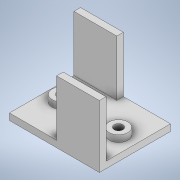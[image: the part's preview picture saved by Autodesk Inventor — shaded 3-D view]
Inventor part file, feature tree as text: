
AUTODESK INVENTOR PART (.ipt)
format: ipt  version: 2020 (Build 240168000, 168)  size: 171,520 bytes
history: native  units: in
note: dims shown in document units (in); Inventor stores cm internally (conversion verified against a paired STEP export)
features: extrude x7, sketch x7
ambient origin geometry x8: Origin, YZ Plane, XZ Plane, XY Plane, X Axis, Y Axis, Z Axis, Center Point
bodies: Solid1 (feature_tree)
feature tree (14):
  extrude  "Extrusion1"  Depth=1.2756in
  extrude  "Extrusion3"  Depth=0.1181in
  extrude  "Extrusion4"  Depth=1.0in TaperAngle=0.0deg
  extrude  "Extrusion5"  Depth=0.1181in TaperAngle=0.0deg
  extrude  "Extrusion6"  Depth=0.1181in TaperAngle=0.0deg
  extrude  "Extrusion7"  Depth=0.3346in
  extrude  "Extrusion8"  Depth=0.1181in
  sketch  "Sketch1"  dims[d0=1.6142in d1=1.2756in]
  sketch  "Sketch3"  dims[d2=0.1181in d3=0.0in d8=0.1181in]
  sketch  "Sketch4"  dims[d9=0.1181in d10=1.0in d11=0.0in]
  sketch  "Sketch5"  dims[d12=0.8465in d13=0.1181in d14=0.0in]
  sketch  "Sketch6"  dims[d15=0.8465in d16=0.1181in d17=0.0in]
  sketch  "Sketch7"  dims[d20=0.3346in d21=0.3346in]
  sketch  "Sketch8"  dims[d22=0.1181in d23=0.0in d24=0.1575in d25=0.1575in d26=0.2362in d27=0.0in d28=0.2362in d29=0.2362in d30=0.1181in d31=0.0in]
